FCSTD DOCUMENT  (FreeCAD 0.20R29177 +426 (Git))
Label: gearbox-small
License: All rights reserved
LicenseURL: http://en.wikipedia.org/wiki/All_rights_reserved
objects: Part::Part2DObjectPython×4, Part::Extrusion×4, Sketcher::SketchObject×1, PartDesign::Body×1
note: 10 computed .brp shape members not serialized (recipe doc carries the construction recipe); baked Part::Feature solids carry a one-line shape summary decoded from their .brp

FEATURE [Sketcher::SketchObject] Sketch
  FullyConstrained = false
  MapMode = 5
  Support = -> [XY_Plane]
  sketch-geometry (9):
    g0: LineSegment StartX=1.50013 StartY=199.994 StartZ=0 EndX=80.869 EndY=189.966 EndZ=0
    g1: LineSegment StartX=80.869 StartY=189.966 StartZ=0 EndX=79.3689 EndY=-10.0287 EndZ=0
    g2: LineSegment StartX=79.3689 StartY=-10.0287 StartZ=0 EndX=0 EndY=-1.8e-15 EndZ=0
    g3: LineSegment StartX=0 StartY=0 StartZ=0 EndX=-79.3689 EndY=10.0287 EndZ=0
    g4: LineSegment StartX=-79.3689 StartY=10.0287 StartZ=0 EndX=-77.8688 EndY=210.023 EndZ=0
    g5: LineSegment StartX=-77.8688 StartY=210.023 StartZ=0 EndX=1.50013 EndY=199.994 EndZ=0
    g6: LineSegment StartX=1.50013 StartY=199.994 StartZ=0 EndX=0 EndY=0 EndZ=0
    g7: LineSegment StartX=105.825 StartY=-129.719 StartZ=0 EndX=203.217 EndY=-260.874 EndZ=0
    g8: LineSegment StartX=1.50013 StartY=199.994 StartZ=0 EndX=2e-16 EndY=499.991 EndZ=0
  constraints (20):
    c: Coincident(g2,g1)
    c: Equal(g2,g0)
    c: Distance(g2) = 80
    c: Coincident(g3,g2)
    c: Equal(g3,g2)
    c: Parallel(g3,g2)
    c: Coincident(g2,g-1)
    c: Coincident(g4,g3)
    c: Coincident(g5,g4)
    c: Coincident(g5,g0)
    c: Parallel(g0,g5)
    c: Parallel(g5,g3)
    c: Equal(g5,g3)
    c: Distance(g4) = 200
    c: Coincident(g6,g0)
    c: Coincident(g6,g2)
    c: Coincident(g8,g0)
    c: PointOnObject(g8,g-2)
    c: Distance(g8) = 300
    c: Coincident(g0,g1)
FEATURE [Part::Part2DObjectPython] InvoluteGear  # Draft 2D object (typed FeaturePython)
  ExternalGear = true
  HighPrecision = true
  Modules = 1
  NumberOfTeeth = 39
  PressureAngle = 20
FEATURE [Part::Extrusion] Extrude
  Base = -> InvoluteGear
  Dir = (0,0,1)
  DirMode = 2
  FaceMakerClass = Part::FaceMakerBullseye
  LengthFwd = 15
  LengthRev = 0
  Solid = true
  Symmetric = false
FEATURE [Part::Part2DObjectPython] InvoluteGear001  # Draft 2D object (typed FeaturePython)
  ExternalGear = true
  HighPrecision = true
  Modules = 1
  NumberOfTeeth = 95
  PressureAngle = 20
FEATURE [PartDesign::Body] Body
  Group = -> [Sketch,InvoluteGear,InvoluteGear001]
  Origin = -> Origin
FEATURE [Part::Extrusion] Extrude001
  Base = -> InvoluteGear001
  Dir = (0,0,1)
  DirMode = 2
  FaceMakerClass = Part::FaceMakerBullseye
  LengthFwd = 15
  LengthRev = 0
  Placement = pos=(0,0,30) rot=(0,0,1;0rad)
  Solid = true
  Symmetric = false
FEATURE [Part::Part2DObjectPython] InvoluteGear002  # Draft 2D object (typed FeaturePython)
  ExternalGear = true
  HighPrecision = true
  Modules = 1
  NumberOfTeeth = 39
  PressureAngle = 20
FEATURE [Part::Extrusion] Extrude002  label="small-gear-2"
  Base = -> InvoluteGear002
  Dir = (0,0,1)
  DirMode = 2
  FaceMakerClass = Part::FaceMakerBullseye
  LengthFwd = 15
  LengthRev = 0
  Placement = pos=(100,0,30) rot=(0,0,1;0rad)
  Solid = true
  Symmetric = false
FEATURE [Part::Part2DObjectPython] InvoluteGear003  # Draft 2D object (typed FeaturePython)
  ExternalGear = true
  HighPrecision = true
  Modules = 1
  NumberOfTeeth = 95
  PressureAngle = 20
FEATURE [Part::Extrusion] Extrude003
  Base = -> InvoluteGear003
  Dir = (0,0,1)
  DirMode = 2
  FaceMakerClass = Part::FaceMakerBullseye
  LengthFwd = 15
  LengthRev = 0
  Placement = pos=(100,0,0) rot=(0,0,1;0rad)
  Solid = true
  Symmetric = false
